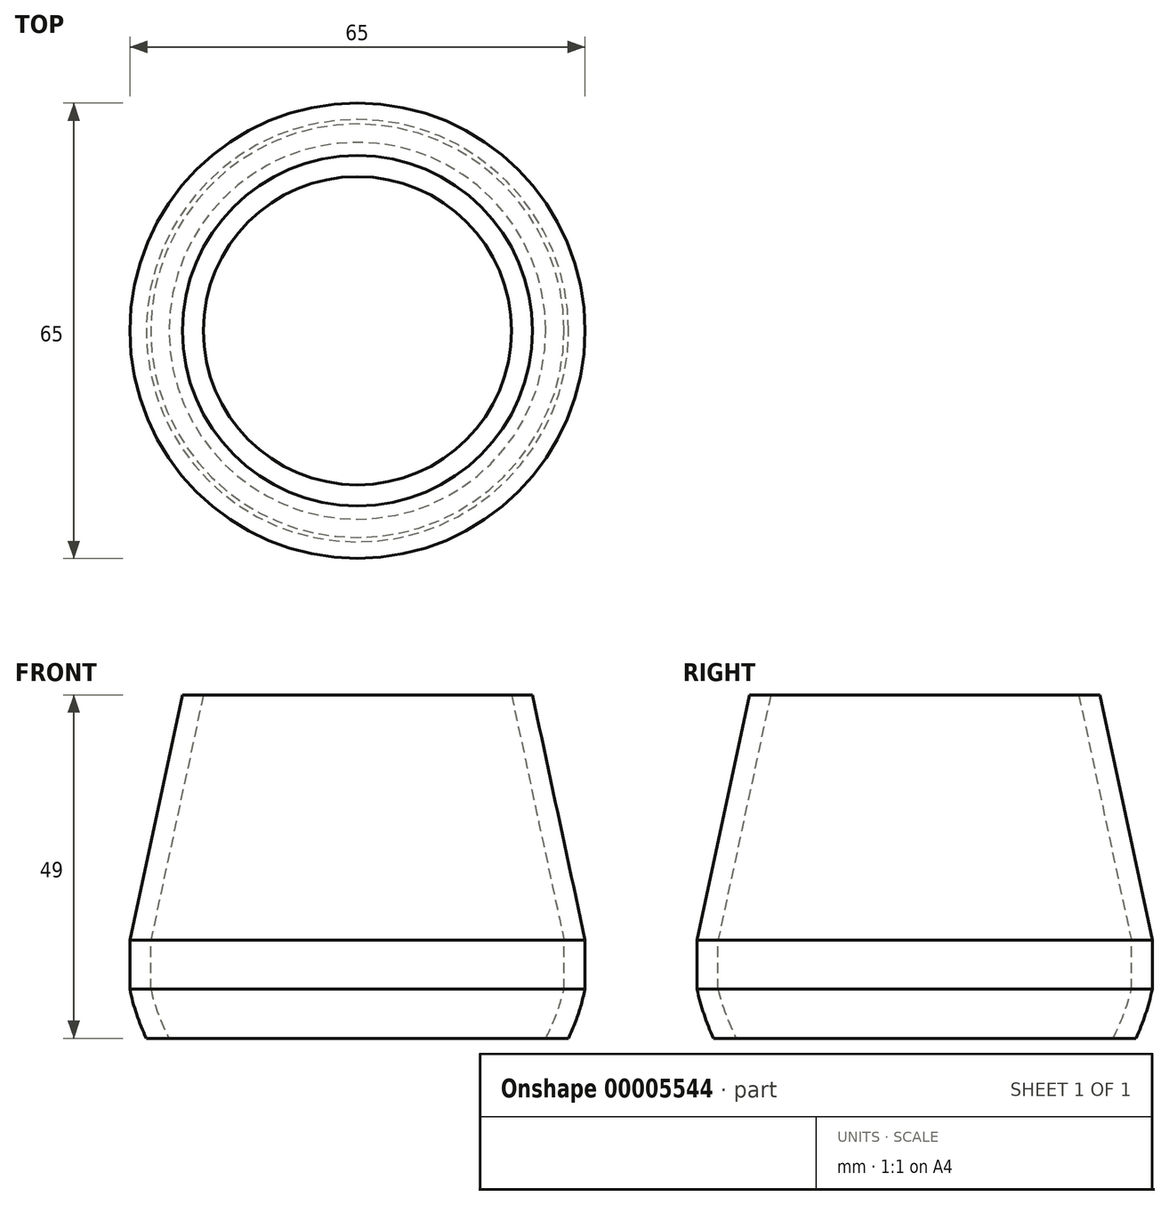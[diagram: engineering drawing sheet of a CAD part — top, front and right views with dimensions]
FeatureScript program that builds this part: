
annotation { "Feature Type Name" : "Feature", "Feature Type Description" : "" }
export const myFeature = defineFeature(function(context is Context, id is Id, definition is map)
    precondition{}
    {
        {
            var Q0;
            Q0=qCreatedBy(makeId("Front.planeOp"),FACE);
            var sketch = newSketch(context, id + "F0", { "sketchPlane" : qUnion([Q0])});
            skLineSegment(sketch, "E0", {"start": v(-25, 35) * mm, "end": v(-22, 35) * mm});
            skLineSegment(sketch, "E1", {"start": v(-22, 35) * mm, "end": v(-29.5, 0) * mm});
            skLineSegment(sketch, "E2", {"start": v(-29.5, 0) * mm, "end": v(-29.5, -7) * mm});
            skLineSegment(sketch, "E3", {"start": v(-32.5, -7) * mm, "end": v(-32.5, 0) * mm});
            skLineSegment(sketch, "E4", {"start": v(-32.5, 0) * mm, "end": v(-25, 35) * mm});
            skLineSegment(sketch, "E5", {"start": v(0, 54.21) * mm, "end": v(0, 0) * mm, "construction": true});
            skArc(sketch, "E6", {"start": v(-32.5, -7) * mm, "mid": v(-31.52, -10.57) * mm, "end": v(-30.15, -14) * mm});
            skArc(sketch, "E7", {"start": v(-29.5, -7) * mm, "mid": v(-28.41, -10.58) * mm, "end": v(-26.9, -14) * mm});
            skLineSegment(sketch, "E8", {"start": v(-30.15, -14) * mm, "end": v(-26.9, -14) * mm});
            skSolve(sketch);
        }
        {
            var Q0;
            Q0=makeQuery(id+"F0.imprint","IMPRINT",FACE,{"disambiguationData":[TD([[makeQuery(id+"F0.imprint","IMPRINT",EDGE,{"derivedFrom":sQuery(id+"F0.wireOp",EDGE,"E0")}),-1.0]])]});
            var Q1;
            Q1=sQuery(id+"F0.wireOp",EDGE,"E5");
            revolve(context, id + "F1", {"entities" : qUnion([Q0]), "axis" : qUnion([Q1]), "revolveType" : RevolveType.FULL});
        }
    });
